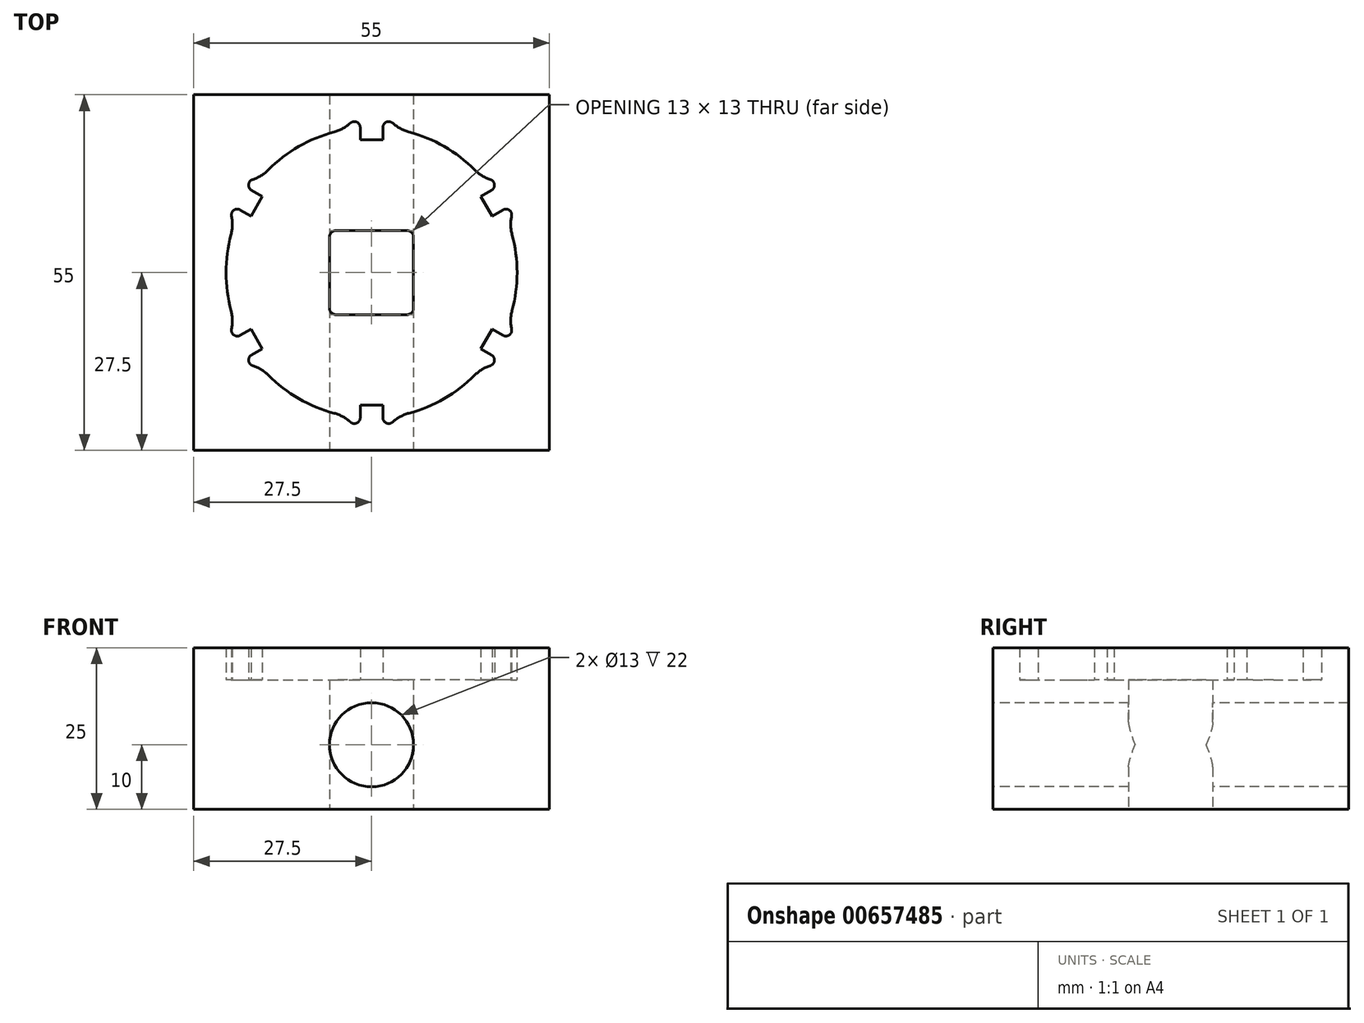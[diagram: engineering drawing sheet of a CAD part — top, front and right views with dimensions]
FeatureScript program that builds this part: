
annotation { "Feature Type Name" : "Feature", "Feature Type Description" : "" }
export const myFeature = defineFeature(function(context is Context, id is Id, definition is map)
    precondition{}
    {
        {
            var Q0;
            Q0=qCreatedBy(makeId("Top.planeOp"),FACE);
            var sketch = newSketch(context, id + "F0", { "sketchPlane" : qUnion([Q0])});
            skArc(sketch, "E0", {"start": v(-3.55, 22.22) * mm, "mid": v(-11.25, 19.49) * mm, "end": v(-17.47, 14.18) * mm});
            skLineSegment(sketch, "E1.top", {"start": v(-1.75, 20.5) * mm, "end": v(1.75, 20.5) * mm});
            skLineSegment(sketch, "E1.left", {"start": v(-1.75, 22.43) * mm, "end": v(-1.75, 20.5) * mm});
            skLineSegment(sketch, "E1.right", {"start": v(1.75, 22.43) * mm, "end": v(1.75, 20.5) * mm});
            skLineSegment(sketch, "E2.bottom", {"start": v(-27.5, 27.5) * mm, "end": v(27.5, 27.5) * mm});
            skLineSegment(sketch, "E2.top", {"start": v(-27.5, -27.5) * mm, "end": v(27.5, -27.5) * mm});
            skLineSegment(sketch, "E2.left", {"start": v(-27.5, 27.5) * mm, "end": v(-27.5, -27.5) * mm});
            skLineSegment(sketch, "E2.right", {"start": v(27.5, 27.5) * mm, "end": v(27.5, -27.5) * mm});
            skArc(sketch, "E3", {"start": v(-1.75, 22.43) * mm, "mid": v(-2.77, 23.34) * mm, "end": v(-3.55, 22.22) * mm});
            skArc(sketch, "E4.MirrorCS", {"start": v(1.75, 22.43) * mm, "mid": v(2.77, 23.34) * mm, "end": v(3.55, 22.22) * mm});
            skArc(sketch, "E5.1.0", {"start": v(-18.55, 12.73) * mm, "mid": v(-18.83, 14.07) * mm, "end": v(-17.47, 14.18) * mm});
            skLineSegment(sketch, "E5.1.1", {"start": v(-18.63, 8.73) * mm, "end": v(-16.88, 11.77) * mm});
            skLineSegment(sketch, "E5.1.2", {"start": v(-18.55, 12.73) * mm, "end": v(-16.88, 11.77) * mm});
            skLineSegment(sketch, "E5.1.3", {"start": v(-20.3, 9.7) * mm, "end": v(-18.63, 8.73) * mm});
            skArc(sketch, "E5.1.4", {"start": v(-20.3, 9.7) * mm, "mid": v(-21.6, 9.27) * mm, "end": v(-21.02, 8.03) * mm});
            skArc(sketch, "E5.2.0", {"start": v(-20.3, -9.7) * mm, "mid": v(-21.6, -9.27) * mm, "end": v(-21.02, -8.03) * mm});
            skLineSegment(sketch, "E5.2.1", {"start": v(-16.88, -11.77) * mm, "end": v(-18.63, -8.73) * mm});
            skLineSegment(sketch, "E5.2.2", {"start": v(-20.3, -9.7) * mm, "end": v(-18.63, -8.73) * mm});
            skLineSegment(sketch, "E5.2.3", {"start": v(-18.55, -12.73) * mm, "end": v(-16.88, -11.77) * mm});
            skArc(sketch, "E5.2.4", {"start": v(-18.55, -12.73) * mm, "mid": v(-18.83, -14.07) * mm, "end": v(-17.47, -14.18) * mm});
            skArc(sketch, "E5.3.0", {"start": v(-1.75, -22.43) * mm, "mid": v(-2.77, -23.34) * mm, "end": v(-3.55, -22.22) * mm});
            skLineSegment(sketch, "E5.3.1", {"start": v(1.75, -20.5) * mm, "end": v(-1.75, -20.5) * mm});
            skLineSegment(sketch, "E5.3.2", {"start": v(-1.75, -22.43) * mm, "end": v(-1.75, -20.5) * mm});
            skLineSegment(sketch, "E5.3.3", {"start": v(1.75, -22.43) * mm, "end": v(1.75, -20.5) * mm});
            skArc(sketch, "E5.3.4", {"start": v(1.75, -22.43) * mm, "mid": v(2.77, -23.34) * mm, "end": v(3.55, -22.22) * mm});
            skArc(sketch, "E5.4.0", {"start": v(18.55, -12.73) * mm, "mid": v(18.83, -14.07) * mm, "end": v(17.47, -14.18) * mm});
            skLineSegment(sketch, "E5.4.1", {"start": v(18.63, -8.73) * mm, "end": v(16.88, -11.77) * mm});
            skLineSegment(sketch, "E5.4.2", {"start": v(18.55, -12.73) * mm, "end": v(16.88, -11.77) * mm});
            skLineSegment(sketch, "E5.4.3", {"start": v(20.3, -9.7) * mm, "end": v(18.63, -8.73) * mm});
            skArc(sketch, "E5.4.4", {"start": v(20.3, -9.7) * mm, "mid": v(21.6, -9.27) * mm, "end": v(21.02, -8.03) * mm});
            skArc(sketch, "E5.5.0", {"start": v(20.3, 9.7) * mm, "mid": v(21.6, 9.27) * mm, "end": v(21.02, 8.03) * mm});
            skLineSegment(sketch, "E5.5.1", {"start": v(16.88, 11.77) * mm, "end": v(18.63, 8.73) * mm});
            skLineSegment(sketch, "E5.5.2", {"start": v(20.3, 9.7) * mm, "end": v(18.63, 8.73) * mm});
            skLineSegment(sketch, "E5.5.3", {"start": v(18.55, 12.73) * mm, "end": v(16.88, 11.77) * mm});
            skArc(sketch, "E5.5.4", {"start": v(18.55, 12.73) * mm, "mid": v(18.83, 14.07) * mm, "end": v(17.47, 14.18) * mm});
            skArc(sketch, "E6.trimOffspring", {"start": v(17.47, 14.18) * mm, "mid": v(11.25, 19.49) * mm, "end": v(3.55, 22.22) * mm});
            skArc(sketch, "E7.trimOffspring", {"start": v(21.02, -8.03) * mm, "mid": v(22.5, 0) * mm, "end": v(21.02, 8.03) * mm});
            skArc(sketch, "E8.trimOffspring", {"start": v(-21.02, 8.03) * mm, "mid": v(-22.5, 0) * mm, "end": v(-21.02, -8.03) * mm});
            skArc(sketch, "E9.trimOffspring", {"start": v(-17.47, -14.18) * mm, "mid": v(-11.25, -19.49) * mm, "end": v(-3.55, -22.22) * mm});
            skArc(sketch, "E10.trimOffspring", {"start": v(3.55, -22.22) * mm, "mid": v(11.25, -19.49) * mm, "end": v(17.47, -14.18) * mm});
            skLineSegment(sketch, "E11.bottom", {"start": v(6.5, 6.5) * mm, "end": v(-6.5, 6.5) * mm});
            skLineSegment(sketch, "E11.top", {"start": v(6.5, -6.5) * mm, "end": v(-6.5, -6.5) * mm});
            skLineSegment(sketch, "E11.left", {"start": v(6.5, 6.5) * mm, "end": v(6.5, -6.5) * mm});
            skLineSegment(sketch, "E11.right", {"start": v(-6.5, 6.5) * mm, "end": v(-6.5, -6.5) * mm});
            skSolve(sketch);
        }
        {
            var Q0;
            Q0=makeQuery(id+"F0.imprint","IMPRINT",FACE,{"disambiguationData":[TD([[makeQuery(id+"F0.imprint","IMPRINT",EDGE,{"derivedFrom":sQuery(id+"F0.wireOp",EDGE,"r3nMNNaN-krWu-wPep-XbRl-0Ppc3XhwaBKd")}),1.0]])]});
            var Q1;
            {var subQ0=sQuery(id+"F0.wireOp",EDGE,"d0184fe7-3e6f-46e7-b22d-c3bf222a9851.1.0");Q1=makeQuery(id+"F0.imprint","IMPRINT",FACE,{"disambiguationData":[TD([[makeQuery(id+"F0.imprint","IMPRINT",EDGE,{"derivedFrom":subQ0}),1.0]])]});}
            var Q2;
            {var subQ0=sQuery(id+"F0.wireOp",EDGE,"d0184fe7-3e6f-46e7-b22d-c3bf222a9851.2.0");Q2=makeQuery(id+"F0.imprint","IMPRINT",FACE,{"disambiguationData":[TD([[makeQuery(id+"F0.imprint","IMPRINT",EDGE,{"derivedFrom":subQ0}),1.0]])]});}
            var Q3;
            {var subQ0=sQuery(id+"F0.wireOp",EDGE,"d0184fe7-3e6f-46e7-b22d-c3bf222a9851.3.0");Q3=makeQuery(id+"F0.imprint","IMPRINT",FACE,{"disambiguationData":[TD([[makeQuery(id+"F0.imprint","IMPRINT",EDGE,{"derivedFrom":subQ0}),1.0]])]});}
            var Q4;
            {var subQ0=sQuery(id+"F0.wireOp",EDGE,"d0184fe7-3e6f-46e7-b22d-c3bf222a9851.4.0");Q4=makeQuery(id+"F0.imprint","IMPRINT",FACE,{"disambiguationData":[TD([[makeQuery(id+"F0.imprint","IMPRINT",EDGE,{"derivedFrom":subQ0}),1.0]])]});}
            var Q5;
            {var subQ0=sQuery(id+"F0.wireOp",EDGE,"d0184fe7-3e6f-46e7-b22d-c3bf222a9851.5.0");Q5=makeQuery(id+"F0.imprint","IMPRINT",FACE,{"disambiguationData":[TD([[makeQuery(id+"F0.imprint","IMPRINT",EDGE,{"derivedFrom":subQ0}),1.0]])]});}
            var Q6;
            Q6=makeQuery(id+"F0.imprint","IMPRINT",FACE,{"disambiguationData":[TD([[makeQuery(id+"F0.imprint","IMPRINT",EDGE,{"derivedFrom":sQuery(id+"F0.wireOp",EDGE,"E1.top")}),1.0]])]});
            var Q7;
            Q7=makeQuery(id+"F0.imprint","IMPRINT",FACE,{"disambiguationData":[TD([[makeQuery(id+"F0.imprint","IMPRINT",EDGE,{"derivedFrom":sQuery(id+"F0.wireOp",EDGE,"E2.bottom")}),-1.0]])]});
            extrude(context, id + "F1", {"entities" : qUnion([Q0, Q1, Q2, Q3, Q4, Q5, Q6, Q7]), "depth" : 25 * mm, "offsetDistance" : 25 * mm});
        }
        {
            var Q0;
            Q0=makeQuery(id+"F0.imprint","IMPRINT",FACE,{"disambiguationData":[TD([[makeQuery(id+"F0.imprint","IMPRINT",EDGE,{"derivedFrom":sQuery(id+"F0.wireOp",EDGE,"OvDwVJYW-SgBX-dwM8-z3pR-tcuNu8yMO1r6.bottom")}),-1.0]])]});
            var Q1;
            {var subQ0=sQuery(id+"F0.wireOp",EDGE,"b311deea-a9d8-4e9a-b7f0-8fce1b82ced0");var subQ1=sQuery(id+"F0.wireOp",EDGE,"E0");var subQ3=makeQuery(id+"F0.imprint","INTERSECT",VERTEX,{"disambiguationData":[OD(1.0)],"derivedFrom":[subQ1,subQ0]});Q1=makeQuery(id+"F0.imprint","IMPRINT",FACE,{"disambiguationData":[TD([[makeQuery(id+"F0.imprint","IMPRINT",EDGE,{"disambiguationData":[TD([[subQ3,1.0]])],"derivedFrom":subQ1}),-1.0]])]});}
            var Q2;
            {var subQ0=sQuery(id+"F0.wireOp",EDGE,"3b10c52a-fb02-45d4-b1bd-004931deaec10.MirrorCS");var subQ1=sQuery(id+"F0.wireOp",EDGE,"E0");var subQ3=makeQuery(id+"F0.imprint","INTERSECT",VERTEX,{"disambiguationData":[OD(1.0)],"derivedFrom":[subQ1,subQ0]});Q2=makeQuery(id+"F0.imprint","IMPRINT",FACE,{"disambiguationData":[TD([[makeQuery(id+"F0.imprint","IMPRINT",EDGE,{"disambiguationData":[TD([[subQ3,-1.0]])],"derivedFrom":subQ1}),-1.0]])]});}
            var Q3;
            Q3=makeQuery(id+"F0.imprint","IMPRINT",FACE,{"disambiguationData":[TD([[makeQuery(id+"F0.imprint","IMPRINT",EDGE,{"derivedFrom":sQuery(id+"F0.wireOp",EDGE,"E0")}),1.0]])]});
            extrude(context, id + "F2", {"entities" : qUnion([Q0, Q1, Q2, Q3]), "operationType" : NewBodyOperationType.ADD, "depth" : 20 * mm, "offsetDistance" : 25 * mm});
        }
        {
            var Q0;
            Q0=makeQuery(id+"F1.opExtrude","SWEPT_EDGE",EDGE,{"disambiguationData":[OSD([sQuery(id+"F0.wireOp",EDGE,"E5.2.0"),sQuery(id+"F0.wireOp",EDGE,"E8.trimOffspring")])]});
            var Q1;
            Q1=makeQuery(id+"F1.opExtrude","SWEPT_EDGE",EDGE,{"disambiguationData":[OSD([sQuery(id+"F0.wireOp",EDGE,"E5.1.4"),sQuery(id+"F0.wireOp",EDGE,"E8.trimOffspring")])]});
            var Q2;
            Q2=makeQuery(id+"F1.opExtrude","SWEPT_EDGE",EDGE,{"disambiguationData":[OSD([sQuery(id+"F0.wireOp",EDGE,"E0"),sQuery(id+"F0.wireOp",EDGE,"E5.1.0")])]});
            var Q3;
            Q3=makeQuery(id+"F1.opExtrude","SWEPT_EDGE",EDGE,{"disambiguationData":[OSD([sQuery(id+"F0.wireOp",EDGE,"E0"),sQuery(id+"F0.wireOp",EDGE,"E3")])]});
            var Q4;
            Q4=makeQuery(id+"F1.opExtrude","SWEPT_EDGE",EDGE,{"disambiguationData":[OSD([sQuery(id+"F0.wireOp",EDGE,"E5.2.4"),sQuery(id+"F0.wireOp",EDGE,"E9.trimOffspring")])]});
            var Q5;
            Q5=makeQuery(id+"F1.opExtrude","SWEPT_EDGE",EDGE,{"disambiguationData":[OSD([sQuery(id+"F0.wireOp",EDGE,"E5.3.0"),sQuery(id+"F0.wireOp",EDGE,"E9.trimOffspring")])]});
            var Q6;
            Q6=makeQuery(id+"F1.opExtrude","SWEPT_EDGE",EDGE,{"disambiguationData":[OSD([sQuery(id+"F0.wireOp",EDGE,"E5.5.4"),sQuery(id+"F0.wireOp",EDGE,"E6.trimOffspring")])]});
            var Q7;
            Q7=makeQuery(id+"F1.opExtrude","SWEPT_EDGE",EDGE,{"disambiguationData":[OSD([sQuery(id+"F0.wireOp",EDGE,"E5.5.0"),sQuery(id+"F0.wireOp",EDGE,"E7.trimOffspring")])]});
            var Q8;
            Q8=makeQuery(id+"F1.opExtrude","SWEPT_EDGE",EDGE,{"disambiguationData":[OSD([sQuery(id+"F0.wireOp",EDGE,"E5.4.4"),sQuery(id+"F0.wireOp",EDGE,"E7.trimOffspring")])]});
            var Q9;
            Q9=makeQuery(id+"F1.opExtrude","SWEPT_EDGE",EDGE,{"disambiguationData":[OSD([sQuery(id+"F0.wireOp",EDGE,"E5.4.0"),sQuery(id+"F0.wireOp",EDGE,"E10.trimOffspring")])]});
            var Q10;
            Q10=makeQuery(id+"F1.opExtrude","SWEPT_EDGE",EDGE,{"disambiguationData":[OSD([sQuery(id+"F0.wireOp",EDGE,"E5.3.4"),sQuery(id+"F0.wireOp",EDGE,"E10.trimOffspring")])]});
            var Q11;
            Q11=makeQuery(id+"F1.opExtrude","SWEPT_EDGE",EDGE,{"disambiguationData":[OSD([sQuery(id+"F0.wireOp",EDGE,"E4.MirrorCS"),sQuery(id+"F0.wireOp",EDGE,"E6.trimOffspring")])]});
            fillet(context, id + "F3", {"entities" : qUnion([Q0, Q1, Q2, Q3, Q4, Q5, Q6, Q7, Q8, Q9, Q10, Q11]), "radius" : 6 * mm, "tangentPropagation" : true, "allowEdgeOverflow" : false});
        }
        {
            var Q0;
            Q0=makeQuery(id+"F2.opExtrude","SWEPT_EDGE",EDGE,{"disambiguationData":[OSD([sQuery(id+"F0.wireOp",EDGE,"E11.bottom"),sQuery(id+"F0.wireOp",EDGE,"E11.left")])]});
            var Q1;
            Q1=makeQuery(id+"F2.opExtrude","SWEPT_EDGE",EDGE,{"disambiguationData":[OSD([sQuery(id+"F0.wireOp",EDGE,"E11.bottom"),sQuery(id+"F0.wireOp",EDGE,"E11.right")])]});
            var Q2;
            Q2=makeQuery(id+"F2.opExtrude","SWEPT_EDGE",EDGE,{"disambiguationData":[OSD([sQuery(id+"F0.wireOp",EDGE,"E11.top"),sQuery(id+"F0.wireOp",EDGE,"E11.right")])]});
            var Q3;
            Q3=makeQuery(id+"F2.opExtrude","SWEPT_EDGE",EDGE,{"disambiguationData":[OSD([sQuery(id+"F0.wireOp",EDGE,"E11.top"),sQuery(id+"F0.wireOp",EDGE,"E11.left")])]});
            fillet(context, id + "F4", {"entities" : qUnion([Q0, Q1, Q2, Q3]), "radius" : 1 * mm, "tangentPropagation" : true, "allowEdgeOverflow" : false});
        }
        {
            var Q0;
            Q0=makeQuery(id+"F1.opExtrude","SWEPT_FACE",FACE,{"disambiguationData":[OSD([sQuery(id+"F0.wireOp",EDGE,"E2.top")])]});
            var sketch = newSketch(context, id + "F5", { "sketchPlane" : qUnion([Q0])});
            skCircle(sketch, "E12", {"center": v(0, 10) * mm, "radius": 6.5 * mm});
            skSolve(sketch);
        }
        {
            var Q0;
            Q0=makeQuery(id+"F5.imprint","IMPRINT",FACE,{"disambiguationData":[TD([[makeQuery(id+"F5.imprint","IMPRINT",EDGE,{"derivedFrom":sQuery(id+"F5.wireOp",EDGE,"E12")}),1.0]])]});
            extrude(context, id + "F6", {"entities" : qUnion([Q0]), "operationType" : NewBodyOperationType.REMOVE, "endBound" : BoundingType.THROUGH_ALL, "oppositeDirection" : true, "depth" : 25 * mm, "offsetDistance" : 25 * mm});
        }
    });
